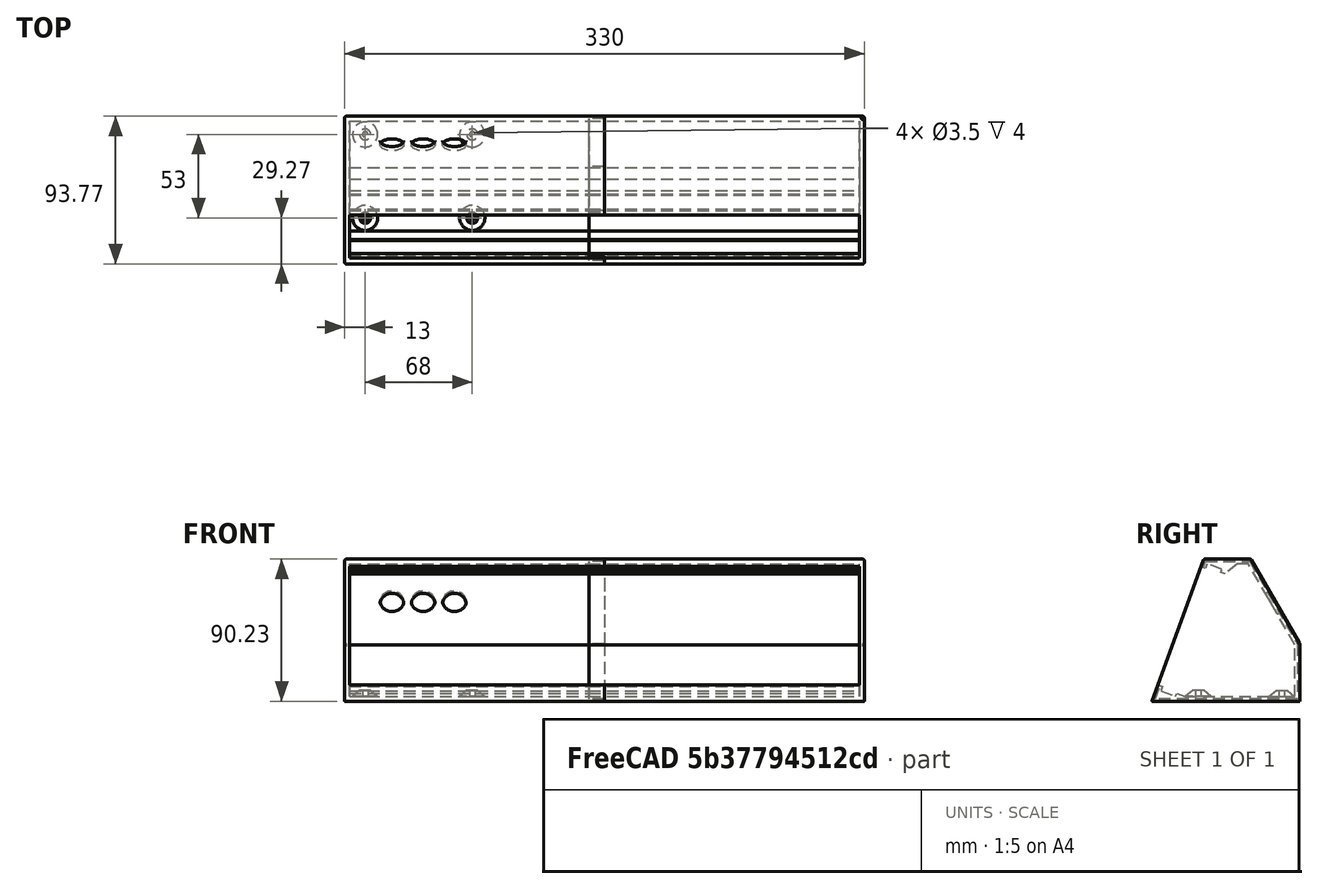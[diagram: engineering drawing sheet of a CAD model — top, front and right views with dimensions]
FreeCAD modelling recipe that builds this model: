
FCSTD DOCUMENT  (FreeCAD 1.0R39109 (Git))
Label: Unibody
License: All rights reserved
LicenseURL: https://en.wikipedia.org/wiki/All_rights_reserved
objects: Sketcher::SketchObject×11, PartDesign::Plane×8, PartDesign::Pocket×6, PartDesign::Fillet×5, PartDesign::Body×3, PartDesign::SubShapeBinder×2, PartDesign::Mirrored×2, PartDesign::FeatureBase×2, Spreadsheet::Sheet×1, PartDesign::Pad×1, PartDesign::AdditiveCone×1, Mesh::Feature×1, PartDesign::Hole×1, PartDesign::MultiTransform×1
note: 87 computed .brp shape members not serialized (recipe doc carries the construction recipe); baked Part::Feature solids carry a one-line shape summary decoded from their .brp

FEATURE [Sketcher::SketchObject] Sketch  label="ProfileMasterSketch"
  ArcFitTolerance = 1e-06
  AttachmentSupport = -> [YZ_Plane]
  FullyConstrained = true
  MakeInternals = false
  MapMode = 5
  Placement = pos=(0,0,0) rot=(0.57735,0.57735,0.57735;2.0944rad)
  expr: Constraints[25] = 90 deg + <<HousingSS>>.screen_angle
  expr: Constraints[35] = <<HousingSS>>.case_thickness
  expr: Constraints[36] = <<HousingSS>>.case_thickness
  expr: Constraints[37] = <<HousingSS>>.case_thickness
  expr: Constraints[38] = <<HousingSS>>.case_thickness
  expr: Constraints[39] = <<HousingSS>>.case_thickness
  expr: Constraints[40] = <<HousingSS>>.case_thickness
  expr: Constraints[41] = <<HousingSS>>.case_thickness
  expr: Constraints[44] = <<HousingSS>>.case_thickness
  expr: Constraints[45] = <<HousingSS>>.case_thickness
  expr: Constraints[46] = 90 deg - <<HousingSS>>.screen_angle
  expr: Constraints[47] = <<HousingSS>>.screen_assembly_depth
  expr: Constraints[48] = <<HousingSS>>.screen_assembly_depth
  expr: Constraints[50] = <<HousingSS>>.back_support_face_height
  expr: Constraints[51] = <<HousingSS>>.back_support_face_height
  expr: Constraints[53] = <<HousingSS>>.case_thickness
  expr: Constraints[54] = <<HousingSS>>.screen_height
  expr: Constraints[56] = <<HousingSS>>.back_angle + 90 deg
  expr: Constraints[60] = <<HousingSS>>.case_thickness
  expr: Constraints[61] = <<HousingSS>>.case_thickness
  expr: Constraints[62] = <<HousingSS>>.case_thickness
  expr: Constraints[63] = <<HousingSS>>.top_depth
  expr: Constraints[64] = <<HousingSS>>.back_bay_depth
  expr: Constraints[66] = <<HousingSS>>.case_thickness
  sketch-geometry (24):
    g0: LineSegment StartX=-60.9314 StartY=90.2338 StartZ=0 EndX=-30.9314 EndY=90.2338 EndZ=0
    g1: LineSegment StartX=-30.9314 StartY=90.2338 StartZ=0 EndX=0 EndY=36.659 EndZ=0
    g2: LineSegment StartX=0 StartY=36.659 StartZ=0 EndX=0 EndY=0 EndZ=0
    g3: LineSegment StartX=0 StartY=0 StartZ=0 EndX=-93.7738 EndY=0 EndZ=0
    g4: LineSegment StartX=-3 StartY=35.8551 StartZ=0 EndX=-3 EndY=3 EndZ=0
    g5: LineSegment StartX=-88.2445 StartY=6.4202 StartZ=0 EndX=-87.2185 EndY=9.23928 EndZ=0
    g6: LineSegment StartX=-87.2185 StartY=9.23928 StartZ=0 EndX=-90.0376 EndY=10.2653 EndZ=0
    g7: LineSegment StartX=-90.0376 StartY=10.2653 StartZ=0 EndX=-93.7738 EndY=0 EndZ=0
    g8: LineSegment StartX=-58.8308 StartY=87.2338 StartZ=0 EndX=-59.8569 EndY=84.4147 EndZ=0
    g9: LineSegment StartX=-59.8569 StartY=84.4147 StartZ=0 EndX=-62.6759 EndY=85.4407 EndZ=0
    g10: LineSegment StartX=-78.8476 StartY=3 StartZ=0 EndX=-88.2445 EndY=6.4202 EndZ=0
    g11: LineSegment StartX=-78.1636 StartY=4.87939 StartZ=0 EndX=-78.8476 EndY=3 EndZ=0
    g12: LineSegment StartX=-93.7738 StartY=0 StartZ=0 EndX=-90.0376 EndY=10.2653 EndZ=0
    g13: LineSegment [constr] StartX=-90.0376 StartY=10.2653 StartZ=0 EndX=-62.6759 EndY=85.4407 EndZ=0
    g14: LineSegment StartX=-62.6759 StartY=85.4407 StartZ=0 EndX=-60.9314 EndY=90.2338 EndZ=0
    g15: LineSegment StartX=-50.1179 StartY=81.9342 StartZ=0 EndX=-49.4339 EndY=83.8136 EndZ=0
    g16: LineSegment StartX=-49.4339 StartY=83.8136 StartZ=0 EndX=-58.8308 EndY=87.2338 EndZ=0
    g17: LineSegment StartX=-32.6635 StartY=87.2338 StartZ=0 EndX=-3 EndY=35.8551 EndZ=0
    g18: LineSegment StartX=-3 StartY=3 StartZ=0 EndX=-73 EndY=3 EndZ=0
    g19: LineSegment StartX=-73 StartY=3 StartZ=0 EndX=-78.1636 EndY=4.87939 EndZ=0
    g20: LineSegment StartX=-39.7602 StartY=87.2338 StartZ=0 EndX=-32.6635 EndY=87.2338 EndZ=0
    g21: LineSegment [constr] StartX=-32.6635 StartY=87.2338 StartZ=0 EndX=-30.0654 EndY=88.7338 EndZ=0
    g22: LineSegment StartX=-50.1179 StartY=81.9342 StartZ=0 EndX=-47.2988 EndY=80.9081 EndZ=0
    g23: LineSegment StartX=-47.2988 StartY=80.9081 StartZ=0 EndX=-39.7602 EndY=87.2338 EndZ=0
  constraints (69):
    c: Horizontal(g0)
    c: Coincident(g0,g1)
    c: PointOnObject(g1,g-2)
    c: Coincident(g1,g2)
    c: Coincident(g2,g-1)
    c: Coincident(g2,g3)
    c: PointOnObject(g3,g-1)
    c: Coincident(g3,g12)
    c: Coincident(g14,g0)
    c: Coincident(g17,g4)
    c: Coincident(g4,g18)
    c: Coincident(g10,g5)
    c: Coincident(g5,g6)
    c: Coincident(g6,g7)
    c: Coincident(g7,g3)
    c: Coincident(g22,g15)
    c: Coincident(g16,g8)
    c: Coincident(g8,g9)
    c: Coincident(g11,g10)
    c: Coincident(g19,g11)
    c: Coincident(g12,g13)
    c: PointOnObject(g9,g12)
    c: Coincident(g13,g14)
    c: Coincident(g13,g9)
    c: Coincident(g12,g6)
    c: Angle(g14,g0) = 1.91986
    c: Angle(g13,g9) = 1.5708
    c: Parallel(g8,g14)
    c: Angle(g7,g6) = 1.5708
    c: Angle(g6,g5) = 1.5708
    c: Angle(g10,g5) = 1.5708
    c: Coincident(g15,g16)
    c: Coincident(g18,g19)
    c: Angle(g11,g10) = 1.5708
    c: Parallel(g17,g1)
    c: DistanceY(g17,g0) = 3
    c: DistanceX(g4,g1) = 3
    c: DistanceX(g4,g2) = 3
    c: DistanceY(g-1,g18) = 3
    c: DistanceY(g-1,g4) = 3
    c: Distance(g6) = 3
    c: Distance(g9) = 3
    c: Angle(g8,g16) = 1.5708
    c: Angle(g16,g15) = 1.5708
    c: DistanceY(g8,g0) = 3
    c: DistanceY(g-1,g10) = 3
    c: Angle(g3,g13) = 1.22173
    c: Distance(g10) = 10
    c: Distance(g16) = 10
    c: Angle(g11,g19) = 1.5708
    c: Distance(g11) = 2
    c: Distance(g15) = 2
    c: Coincident(g23,g20)
    c: DistanceY(g23,g0) = 3
    c: Distance(g13) = 80
    c: Coincident(g20,g17)
    c: Angle(g20,g17) = 2.0944
    c: Coincident(g21,g17)
    c: PointOnObject(g21,g1)
    c: Angle(g17,g21) = 1.5708
    c: Distance(g21) = 3
    c: Distance(g5) = 3
    c: Distance(g8) = 3
    c: Distance(g0) = 30
    c: Distance(g18) = 70
    c: Coincident(g22,g23)
    c: Distance(g22) = 3
    c: Angle(g22,g15) = 1.5708
    c: Angle(g23,g22) = 2.0944
FEATURE [Spreadsheet::Sheet] Spreadsheet  label="HousingSS"
  cells = B1='screen_angle; C1='case_thickness; D1='screen_assembly_depth; E1='screen_height; F1='back_support_face_height; G1='back_angle; H1='top_depth; I1='back_edge_height; J1='housing_width; K1='opening_width; L1='back_bay_depth; M1='split_offset; N1='screw_split_offset; O1='split_overlap; P1='split_middle; Q1='breakout_mount_diameter; R1='button_diameter; S1='button_spacing; T1='pin_pitch; U1='breakout_mount_support; V1='threaded_insert_diameter; W1='threaded_insert_depth; A2==hiddenref(Body.Configuration.String); B2(screen_angle)==.B3; C2(case_thickness)==.C3; D2(screen_assembly_depth)==.D3; E2(screen_height)==.E3; F2(back_support_face_height)==.F3; G2(back_angle)==.G3; H2(top_depth)==.H3; I2(back_edge_height)==.I3; J2(housing_width)==.J3; K2(opening_width)==.K3; L2(back_bay_depth)==.L3; M2(split_offset)==.M3; N2(screw_split_offset)==.N3; O2(split_overlap)==.O3; P2(split_middle)==.P3; Q2(breakout_mount_diameter)==.Q3; R2(button_diameter)==.R3; S2(button_spacing)==.S3; T2(pin_pitch)==.T3; U2(breakout_mount_support)==.U3; V2(threaded_insert_diameter)==.V3; W2(threaded_insert_depth)==.W3; A3='A; B3==20 deg; C3==3 mm; D3==1 cm; E3==80 mm; F3==2 mm; G3==30 deg; H3==3 cm; I3==30 mm; J3==33 cm; K3==housing_width - case_thickness * 2; L3==70 mm; M3==housing_width / 2; N3==10 mm; O3==1 cm; P3==split_offset + split_overlap / 2; Q3==3 mm; R3==15 mm; S3==button_diameter + mod(button_diameter; pin_pitch) * 1 mm + pin_pitch; T3==2.54 mm; U3==4 mm; V3==5 mm; W3==4 mm
  expr: .cells.Bind.B2.ZZ2 = tuple(.cells; <<B>> + str(hiddenref(Body.Configuration) + 3); <<ZZ>> + str(hiddenref(Body.Configuration) + 3))
FEATURE [Sketcher::SketchObject] Sketch001  label="OuterBodySketch"
  ArcFitTolerance = 1e-06
  AttachmentSupport = -> [YZ_Plane]
  ExternalGeometry = -> [Sketch]
  FullyConstrained = true
  MakeInternals = false
  MapMode = 5
  Placement = pos=(0,0,0) rot=(0.57735,0.57735,0.57735;2.0944rad)
  sketch-geometry (5):
    g0: LineSegment StartX=-60.9314 StartY=90.2338 StartZ=0 EndX=-93.7738 EndY=0 EndZ=0
    g1: LineSegment StartX=-93.7738 StartY=0 StartZ=0 EndX=0 EndY=0 EndZ=0
    g2: LineSegment StartX=0 StartY=0 StartZ=0 EndX=0 EndY=36.659 EndZ=0
    g3: LineSegment StartX=0 StartY=36.659 StartZ=0 EndX=-30.9314 EndY=90.2338 EndZ=0
    g4: LineSegment StartX=-30.9314 StartY=90.2338 StartZ=0 EndX=-60.9314 EndY=90.2338 EndZ=0
  constraints (10):
    c: Coincident(g0,g-3)
    c: Coincident(g0,g-4)
    c: Coincident(g0,g1)
    c: Coincident(g1,g-1)
    c: Coincident(g1,g2)
    c: Coincident(g2,g-5)
    c: Coincident(g2,g3)
    c: Coincident(g3,g-6)
    c: Coincident(g3,g4)
    c: Coincident(g4,g0)
FEATURE [PartDesign::Pad] Pad  label="OuterBody"
  Direction = (1,0,0)
  Length = 330
  Length2 = 10
  Placement = pos=(0,0,0) rot=(1,1,1;2.0944rad)
  Profile = -> Sketch001
  ReferenceAxis = -> Sketch001 [N_Axis]
  Refine = true
  Suppressed = false
  Type = 0
  expr: Length = <<HousingSS>>.housing_width
FEATURE [PartDesign::Plane] DatumPlane  label="InnerWallPlane"
  AttachmentOffset = pos=(0,0,3) rot=(0,0,1;0rad)
  AttachmentSupport = -> [YZ_Plane]
  Length = 142.172
  MapMode = 5
  Placement = pos=(3,0,0) rot=(0.57735,0.57735,0.57735;2.0944rad)
  ResizeMode = 0
  Width = 138.632
  expr: .AttachmentOffset.Base.z = <<HousingSS>>.case_thickness
FEATURE [Sketcher::SketchObject] Sketch002  label="InnerOpeningSketch"
  ArcFitTolerance = 1e-06
  AttachmentSupport = -> [DatumPlane]
  ExternalGeometry = -> [Sketch]
  FullyConstrained = true
  MakeInternals = false
  MapMode = 5
  Placement = pos=(3,0,0) rot=(0.57735,0.57735,0.57735;2.0944rad)
  sketch-geometry (16):
    g0: LineSegment StartX=-62.6759 StartY=85.4407 StartZ=0 EndX=-90.0376 EndY=10.2653 EndZ=0
    g1: LineSegment StartX=-90.0376 StartY=10.2653 StartZ=0 EndX=-87.2185 EndY=9.23928 EndZ=0
    g2: LineSegment StartX=-87.2185 StartY=9.23928 StartZ=0 EndX=-88.2445 EndY=6.4202 EndZ=0
    g3: LineSegment StartX=-88.2445 StartY=6.4202 StartZ=0 EndX=-78.8476 EndY=3 EndZ=0
    g4: LineSegment StartX=-78.8476 StartY=3 StartZ=0 EndX=-78.1636 EndY=4.87939 EndZ=0
    g5: LineSegment StartX=-78.1636 StartY=4.87939 StartZ=0 EndX=-73 EndY=3 EndZ=0
    g6: LineSegment StartX=-73 StartY=3 StartZ=0 EndX=-3 EndY=3 EndZ=0
    g7: LineSegment StartX=-3 StartY=3 StartZ=0 EndX=-3 EndY=35.8551 EndZ=0
    g8: LineSegment StartX=-3 StartY=35.8551 StartZ=0 EndX=-32.6635 EndY=87.2338 EndZ=0
    g9: LineSegment StartX=-32.6635 StartY=87.2338 StartZ=0 EndX=-39.7602 EndY=87.2338 EndZ=0
    g10: LineSegment StartX=-50.1179 StartY=81.9342 StartZ=0 EndX=-49.4339 EndY=83.8136 EndZ=0
    g11: LineSegment StartX=-49.4339 StartY=83.8136 StartZ=0 EndX=-58.8308 EndY=87.2338 EndZ=0
    g12: LineSegment StartX=-58.8308 StartY=87.2338 StartZ=0 EndX=-59.8569 EndY=84.4147 EndZ=0
    g13: LineSegment StartX=-59.8569 StartY=84.4147 StartZ=0 EndX=-62.6759 EndY=85.4407 EndZ=0
    g14: LineSegment StartX=-39.7602 StartY=87.2338 StartZ=0 EndX=-47.2988 EndY=80.9081 EndZ=0
    g15: LineSegment StartX=-47.2988 StartY=80.9081 StartZ=0 EndX=-50.1179 EndY=81.9342 EndZ=0
  constraints (32):
    c: Coincident(g0,g-16)
    c: Coincident(g0,g-4)
    c: Coincident(g0,g1)
    c: Coincident(g1,g-5)
    c: Coincident(g1,g2)
    c: Coincident(g2,g-6)
    c: Coincident(g2,g3)
    c: Coincident(g3,g-7)
    c: Coincident(g3,g4)
    c: Coincident(g4,g-8)
    c: Coincident(g4,g5)
    c: Coincident(g5,g-9)
    c: Coincident(g5,g6)
    c: Coincident(g6,g-10)
    c: Coincident(g6,g7)
    c: Coincident(g7,g-11)
    c: Coincident(g7,g8)
    c: Coincident(g8,g-12)
    c: Coincident(g8,g9)
    c: Coincident(g15,g-13)
    c: Coincident(g15,g10)
    c: Coincident(g10,g-14)
    c: Coincident(g10,g11)
    c: Coincident(g11,g-15)
    c: Coincident(g11,g12)
    c: Coincident(g12,g-3)
    c: Coincident(g12,g13)
    c: Coincident(g13,g0)
    c: Coincident(g9,g-18)
    c: Coincident(g14,g9)
    c: Coincident(g14,g15)
    c: Coincident(g14,g-17)
FEATURE [PartDesign::Pocket] Pocket
  BaseFeature = -> Pad
  Direction = (-1,0,0)
  Length = 324
  Length2 = 5
  Placement = pos=(0,0,0) rot=(1,1,1;2.0944rad)
  Profile = -> Sketch002
  ReferenceAxis = -> Sketch002 [N_Axis]
  Refine = true
  Reversed = true
  Suppressed = false
  Type = 0
  expr: Length = <<HousingSS>>.opening_width
FEATURE [PartDesign::Plane] DatumPlane001  label="BackSlopeDatumPlane"
  AttachmentOffset = pos=(0,0,0) rot=(1,0,0;1.5708rad)
  AttachmentSupport = -> [Sketch]
  Length = 67.8428
  MapMode = 7
  Placement = pos=(0,-30.9314,90.2338) rot=(1,0,0;2.0944rad)
  ResizeMode = 0
  Width = 177.025
FEATURE [Sketcher::SketchObject] Sketch003  label="SplitCutSketch"
  ArcFitTolerance = 1e-06
  AttachmentSupport = -> [YZ_Plane]
  ExternalGeometry = -> [Sketch]
  FullyConstrained = true
  MakeInternals = false
  MapMode = 5
  Placement = pos=(0,0,0) rot=(0.57735,0.57735,0.57735;2.0944rad)
  expr: Constraints[23] = Sketch.Constraints[25]
  expr: Constraints[25] = Sketch.Constraints[30]
  expr: Constraints[28] = Sketch.Constraints[33]
  expr: Constraints[30] = Sketch.Constraints[35]
  expr: Constraints[31] = Sketch.Constraints[36]
  expr: Constraints[32] = Sketch.Constraints[37]
  expr: Constraints[33] = Sketch.Constraints[38]
  expr: Constraints[34] = Sketch.Constraints[42]
  expr: Constraints[35] = Sketch.Constraints[43]
  expr: Constraints[36] = Sketch.Constraints[44]
  expr: Constraints[37] = Sketch.Constraints[45]
  expr: Constraints[38] = Sketch.Constraints[46]
  expr: Constraints[39] = Sketch.Constraints[47]
  expr: Constraints[40] = Sketch.Constraints[48]
  expr: Constraints[41] = Sketch.Constraints[49]
  expr: Constraints[42] = Sketch.Constraints[50]
  expr: Constraints[43] = Sketch.Constraints[51]
  expr: Constraints[44] = Sketch.Constraints[53]
  expr: Constraints[45] = Sketch.Constraints[54]
  expr: Constraints[47] = Sketch.Constraints[56]
  expr: Constraints[50] = Sketch.Constraints[59]
  expr: Constraints[51] = Sketch.Constraints[60]
  expr: Constraints[52] = Sketch.Constraints[61]
  expr: Constraints[53] = Sketch.Constraints[62]
  expr: Constraints[54] = Sketch.Constraints[63]
  expr: Constraints[55] = Sketch.Constraints[64]
  expr: Constraints[92] = <<HousingSS>>.case_thickness / 2
  sketch-geometry (42):
    g0: LineSegment StartX=-60.9314 StartY=90.2338 StartZ=0 EndX=-30.9314 EndY=90.2338 EndZ=0
    g1: LineSegment StartX=-30.9314 StartY=90.2338 StartZ=0 EndX=0 EndY=36.659 EndZ=0
    g2: LineSegment StartX=0 StartY=36.659 StartZ=0 EndX=0 EndY=0 EndZ=0
    g3: LineSegment StartX=0 StartY=0 StartZ=0 EndX=-93.7738 EndY=0 EndZ=0
    g4: LineSegment StartX=-3 StartY=35.8551 StartZ=0 EndX=-3 EndY=3 EndZ=0
    g5: LineSegment StartX=-88.2445 StartY=6.4202 StartZ=0 EndX=-87.2185 EndY=9.23928 EndZ=0
    g6: LineSegment StartX=-90.0376 StartY=10.2653 StartZ=0 EndX=-93.7738 EndY=0 EndZ=0
    g7: LineSegment StartX=-58.8308 StartY=87.2338 StartZ=0 EndX=-59.8569 EndY=84.4147 EndZ=0
    g8: LineSegment StartX=-78.8476 StartY=3 StartZ=0 EndX=-88.2445 EndY=6.4202 EndZ=0
    g9: LineSegment StartX=-78.1636 StartY=4.87939 StartZ=0 EndX=-78.8476 EndY=3 EndZ=0
    g10: LineSegment StartX=-93.7738 StartY=0 StartZ=0 EndX=-90.0376 EndY=10.2653 EndZ=0
    g11: LineSegment [constr] StartX=-90.0376 StartY=10.2653 StartZ=0 EndX=-62.6759 EndY=85.4407 EndZ=0
    g12: LineSegment StartX=-62.6759 StartY=85.4407 StartZ=0 EndX=-60.9314 EndY=90.2338 EndZ=0
    g13: LineSegment StartX=-50.1179 StartY=81.9342 StartZ=0 EndX=-49.4339 EndY=83.8136 EndZ=0
    g14: LineSegment StartX=-49.4339 StartY=83.8136 StartZ=0 EndX=-58.8308 EndY=87.2338 EndZ=0
    g15: LineSegment StartX=-32.6635 StartY=87.2338 StartZ=0 EndX=-3 EndY=35.8551 EndZ=0
    g16: LineSegment StartX=-3 StartY=3 StartZ=0 EndX=-73 EndY=3 EndZ=0
    g17: LineSegment StartX=-73 StartY=3 StartZ=0 EndX=-78.1636 EndY=4.87939 EndZ=0
    g18: LineSegment StartX=-47.2988 StartY=80.9081 StartZ=0 EndX=-39.7602 EndY=87.2338 EndZ=0
    g19: LineSegment StartX=-39.7602 StartY=87.2338 StartZ=0 EndX=-32.6635 EndY=87.2338 EndZ=0
    g20: LineSegment [constr] StartX=-32.6635 StartY=87.2338 StartZ=0 EndX=-30.0654 EndY=88.7338 EndZ=0
    g21: LineSegment StartX=-59.8569 StartY=84.4147 StartZ=0 EndX=-61.2664 EndY=84.9277 EndZ=0
    g22: LineSegment StartX=-61.2664 StartY=84.9277 StartZ=0 EndX=-62.6759 EndY=85.4407 EndZ=0
    g23: LineSegment StartX=-87.2185 StartY=9.23928 StartZ=0 EndX=-88.628 EndY=9.75231 EndZ=0
    g24: LineSegment StartX=-88.628 StartY=9.75231 StartZ=0 EndX=-90.0376 EndY=10.2653 EndZ=0
    g25: LineSegment [constr] StartX=-58.8308 StartY=87.2338 StartZ=0 EndX=-59.8811 EndY=88.7338 EndZ=0
    g26: LineSegment [constr] StartX=-59.8811 StartY=88.7338 StartZ=0 EndX=-60.9314 EndY=90.2338 EndZ=0
    g27: LineSegment [constr] StartX=-32.6635 StartY=87.2338 StartZ=0 EndX=-31.7975 EndY=88.7338 EndZ=0
    g28: LineSegment [constr] StartX=-31.7975 StartY=88.7338 StartZ=0 EndX=-30.9314 EndY=90.2338 EndZ=0
    g29: LineSegment [constr] StartX=-3 StartY=35.8551 StartZ=0 EndX=-1.5 EndY=36.257 EndZ=0
    g30: LineSegment [constr] StartX=-1.5 StartY=36.257 StartZ=0 EndX=0 EndY=36.659 EndZ=0
    g31: LineSegment StartX=-61.2664 StartY=84.9277 StartZ=0 EndX=-59.8811 EndY=88.7338 EndZ=0
    g32: LineSegment StartX=-59.8811 StartY=88.7338 StartZ=0 EndX=-31.7975 EndY=88.7338 EndZ=0
    g33: LineSegment StartX=-31.7975 StartY=88.7338 StartZ=0 EndX=-1.5 EndY=36.257 EndZ=0
    g34: LineSegment StartX=-1.5 StartY=36.257 StartZ=0 EndX=-1.5 EndY=1.5 EndZ=0
    g35: LineSegment StartX=-91.6316 StartY=1.5 StartZ=0 EndX=-88.628 EndY=9.75231 EndZ=0
    g36: LineSegment [constr] StartX=-88.628 StartY=9.75231 StartZ=0 EndX=-91.6316 EndY=1.5 EndZ=0
    g37: LineSegment [constr] StartX=-91.6316 StartY=1.5 StartZ=0 EndX=-92.1776 EndY=0 EndZ=0
    g38: LineSegment StartX=-91.6316 StartY=1.5 StartZ=0 EndX=-1.5 EndY=1.5 EndZ=0
    g39: LineSegment [constr] StartX=-3 StartY=3 StartZ=0 EndX=-1.5 EndY=1.5 EndZ=0
    g40: LineSegment [constr] StartX=-1.5 StartY=1.5 StartZ=0 EndX=0 EndY=0 EndZ=0
    g41: LineSegment StartX=-50.1179 StartY=81.9342 StartZ=0 EndX=-47.2988 EndY=80.9081 EndZ=0
  constraints (106):
    c: Horizontal(g0)
    c: Coincident(g0,g1)
    c: PointOnObject(g1,g-2)
    c: Coincident(g1,g2)
    c: Coincident(g2,g3)
    c: PointOnObject(g3,g-1)
    c: Coincident(g3,g10)
    c: Coincident(g12,g0)
    c: Coincident(g15,g4)
    c: Coincident(g4,g16)
    c: Coincident(g8,g5)
    c: Coincident(g5,g23)
    c: Coincident(g24,g6)
    c: Coincident(g6,g3)
    c: Coincident(g14,g7)
    c: Coincident(g7,g21)
    c: Coincident(g9,g8)
    c: Coincident(g17,g9)
    c: Coincident(g10,g11)
    c: PointOnObject(g22,g10)
    c: Coincident(g11,g12)
    c: Coincident(g11,g22)
    c: Coincident(g10,g24)
    c: Angle(g12,g0) = 1.91986
    c: Parallel(g7,g12)
    c: Angle(g8,g5) = 1.5708
    c: Coincident(g13,g14)
    c: Coincident(g16,g17)
    c: Angle(g9,g8) = 1.5708
    c: Parallel(g15,g1)
    c: DistanceY(g15,g0) = 3
    c: DistanceX(g4,g1) = 3
    c: DistanceX(g4,g2) = 3
    c: DistanceY(g-1,g16) = 3
    c: Angle(g7,g14) = 1.5708
    c: Angle(g14,g13) = 1.5708
    c: DistanceY(g7,g0) = 3
    c: DistanceY(g-1,g8) = 3
    c: Angle(g3,g11) = 1.22173
    c: Distance(g8) = 10
    c: Distance(g14) = 10
    c: Angle(g9,g17) = 1.5708
    c: Distance(g9) = 2
    c: Distance(g13) = 2
    c: DistanceY(g18,g0) = 3
    c: Distance(g11) = 80
    c: Coincident(g19,g15)
    c: Angle(g19,g15) = 2.0944
    c: Coincident(g20,g15)
    c: PointOnObject(g20,g1)
    c: Angle(g15,g20) = 1.5708
    c: Distance(g20) = 3
    c: Distance(g5) = 3
    c: Distance(g7) = 3
    c: Distance(g0) = 30
    c: Distance(g16) = 70
    c: Coincident(g21,g22)
    c: Distance(g21,g22) = 3
    c: Equal(g21,g22)
    c: Distance(g23,g24) = 3
    c: Equal(g23,g24)
    c: Angle(g23,g5) = 1.5708
    c: Angle(g7,g21) = 1.5708
    c: Angle(g22,g12) = 1.5708
    c: Tangent(g23,g24) = -1.5708
    c: Coincident(g25,g7)
    c: Coincident(g26,g0)
    c: Tangent(g25,g26) = -1.5708
    c: Equal(g26,g25)
    c: Coincident(g27,g15)
    c: Coincident(g28,g0)
    c: Tangent(g27,g28) = -1.5708
    c: Equal(g27,g28)
    c: Coincident(g29,g4)
    c: Coincident(g30,g1)
    c: Tangent(g29,g30) = -1.5708
    c: Equal(g29,g30)
    c: Coincident(g21,g31)
    c: Coincident(g31,g25)
    c: Coincident(g31,g32)
    c: Coincident(g32,g27)
    c: Coincident(g32,g33)
    c: Coincident(g33,g29)
    c: Coincident(g33,g34)
    c: Coincident(g35,g23)
    c: Coincident(g-1,g2)
    c: Angle(g4,g16) = 1.5708
    c: Coincident(g36,g23)
    c: PointOnObject(g37,g3)
    c: Coincident(g36,g37)
    c: Parallel(g36,g6)
    c: Parallel(g37,g6)
    c: DistanceY(g3,g36) = 1.5
    c: Coincident(g35,g36)
    c: Coincident(g38,g35)
    c: Coincident(g38,g34)
    c: Horizontal(g38)
    c: Coincident(g39,g4)
    c: Coincident(g40,g2)
    c: Tangent(g39,g40) = -1.5708
    c: Coincident(g34,g39)
    c: Coincident(g19,g-3)
    c: Coincident(g18,g19)
    c: Coincident(g18,g-4)
    c: Coincident(g41,g13)
    c: Coincident(g41,g18)
FEATURE [PartDesign::SubShapeBinder] Binder
  BindCopyOnChange = 0
  BindMode = 0
  ClaimChildren = false
  Context = -> Body001 [Binder.]
  Fuse = false
  MakeFace = true
  OffsetFill = false
  OffsetIntersection = false
  OffsetJoinType = 0
  OffsetOpenResult = false
  PartialLoad = false
  Refine = true
  Relative = true
  Support = -> [Body[Sketch003.]]
  _Version = 2
FEATURE [PartDesign::SubShapeBinder] Binder001
  BindCopyOnChange = 0
  BindMode = 0
  ClaimChildren = false
  Context = -> Body002 [Binder001.]
  Fuse = false
  MakeFace = true
  OffsetFill = false
  OffsetIntersection = false
  OffsetJoinType = 0
  OffsetOpenResult = false
  PartialLoad = false
  Refine = true
  Relative = true
  Support = -> [Body[Sketch003.]]
  _Version = 2
FEATURE [PartDesign::Plane] DatumPlane004  label="InnerBottomPlane"
  AttachmentOffset = pos=(0,0,3) rot=(0,0,1;0rad)
  AttachmentSupport = -> [XY_Plane]
  Length = 65.4126
  MapMode = 5
  Placement = pos=(0,0,3) rot=(0,0,1;0rad)
  ResizeMode = 0
  Width = 134.186
  expr: .AttachmentOffset.Base.z = <<HousingSS>>.case_thickness
FEATURE [Sketcher::SketchObject] Sketch008  label="BottomMasterSketch"
  ArcFitTolerance = 1e-06
  AttachmentSupport = -> [DatumPlane004]
  ExternalGeometry = -> [Sketch002,Pocket]
  FullyConstrained = true
  MakeInternals = false
  MapMode = 5
  Placement = pos=(0,0,3) rot=(0,0,1;0rad)
  expr: Constraints[27] = <<HousingSS>>.breakout_mount_diameter
  expr: Constraints[28] = <<HousingSS>>.breakout_mount_diameter
  expr: Constraints[29] = 1 cm
  expr: Constraints[31] = <<HousingSS>>.breakout_mount_support
  expr: Constraints[33] = <<HousingSS>>.breakout_mount_support
  expr: Constraints[35] = <<HousingSS>>.breakout_mount_support
  expr: Constraints[37] = <<HousingSS>>.breakout_mount_support
  sketch-geometry (24):
    g0: LineSegment StartX=327 StartY=-3 StartZ=0 EndX=3 EndY=-3 EndZ=0
    g1: LineSegment StartX=3 StartY=-3 StartZ=0 EndX=3 EndY=-73 EndZ=0
    g2: LineSegment StartX=3 StartY=-73 StartZ=0 EndX=327 EndY=-73 EndZ=0
    g3: LineSegment StartX=327 StartY=-73 StartZ=0 EndX=327 EndY=-3 EndZ=0
    g4: Circle CenterX=13 CenterY=-11.5 CenterZ=0 NormalX=0 NormalY=0 NormalZ=1 AngleXU=0 Radius=1.5
    g5: Circle CenterX=13 CenterY=-64.5 CenterZ=0 NormalX=0 NormalY=0 NormalZ=1 AngleXU=0 Radius=1.5
    g6: Circle CenterX=81 CenterY=-11.4999 CenterZ=0 NormalX=0 NormalY=0 NormalZ=1 AngleXU=0 Radius=1.5
    g7: Circle CenterX=81 CenterY=-64.5 CenterZ=0 NormalX=0 NormalY=0 NormalZ=1 AngleXU=0 Radius=1.5
    g8: LineSegment [constr] StartX=13 StartY=-11.5 StartZ=0 EndX=13 EndY=-3 EndZ=0
    g9: LineSegment [constr] StartX=13 StartY=-64.5 StartZ=0 EndX=13 EndY=-73 EndZ=0
    g10: Circle CenterX=13 CenterY=-64.5 CenterZ=0 NormalX=0 NormalY=0 NormalZ=1 AngleXU=0 Radius=2
    g11: Circle CenterX=13 CenterY=-11.5 CenterZ=0 NormalX=0 NormalY=0 NormalZ=1 AngleXU=0 Radius=2
    g12: Circle CenterX=81 CenterY=-11.4999 CenterZ=0 NormalX=0 NormalY=0 NormalZ=1 AngleXU=0 Radius=2
    g13: Circle CenterX=81 CenterY=-64.5 CenterZ=0 NormalX=0 NormalY=0 NormalZ=1 AngleXU=0 Radius=2
    g14: LineSegment [constr] StartX=13 StartY=-11.5 StartZ=0 EndX=13 EndY=-38 EndZ=0
    g15: LineSegment [constr] StartX=13 StartY=-38 StartZ=0 EndX=13 EndY=-64.5 EndZ=0
    g16: LineSegment [constr] StartX=81 StartY=-64.5 StartZ=0 EndX=81 EndY=-38 EndZ=0
    g17: LineSegment [constr] StartX=81 StartY=-38 StartZ=0 EndX=81 EndY=-11.4999 EndZ=0
    g18: LineSegment StartX=13 StartY=-38 StartZ=0 EndX=81 EndY=-38 EndZ=0
    g19: LineSegment [constr] StartX=81 StartY=-11.4999 StartZ=0 EndX=47 EndY=-11.4999 EndZ=0
    g20: LineSegment [constr] StartX=47 StartY=-11.4999 StartZ=0 EndX=13 EndY=-11.5 EndZ=0
    g21: LineSegment [constr] StartX=13 StartY=-64.5 StartZ=0 EndX=47 EndY=-64.5 EndZ=0
    g22: LineSegment [constr] StartX=47 StartY=-64.5 StartZ=0 EndX=81 EndY=-64.5 EndZ=0
    g23: LineSegment StartX=47 StartY=-11.4999 StartZ=0 EndX=47 EndY=-64.5 EndZ=0
  constraints (60):
    c: Coincident(g0,g1)
    c: Coincident(g1,g2)
    c: Coincident(g2,g3)
    c: Coincident(g3,g0)
    c: Horizontal(g0)
    c: Horizontal(g2)
    c: Vertical(g1)
    c: Vertical(g3)
    c: Coincident(g0,g-5)
    c: Coincident(g1,g-3)
    c: Coincident(g14,g4)
    c: Coincident(g15,g5)
    c: Coincident(g21,g5)
    c: Coincident(g22,g7)
    c: Coincident(g22,g16)
    c: Coincident(g17,g6)
    c: Coincident(g17,g19)
    c: Coincident(g20,g4)
    c: Coincident(g8,g4)
    c: PointOnObject(g8,g0)
    c: Vertical(g8)
    c: Coincident(g9,g5)
    c: PointOnObject(g9,g2)
    c: Vertical(g9)
    c: Equal(g8,g9)
    c: Diameter(g7) = 3
    c: Diameter(g6) = 3
    c: Diameter(g4) = 3
    c: Diameter(g5) = 3
    c: Distance(g4,g1) = 10
    c: Coincident(g10,g5)
    c: Diameter(g10) = 4
    c: Coincident(g11,g4)
    c: Diameter(g11) = 4
    c: Coincident(g12,g6)
    c: Diameter(g12) = 4
    c: Coincident(g13,g7)
    c: Diameter(g13) = 4
    c: Coincident(g14,g15)
    c: Vertical(g14)
    c: Vertical(g15)
    c: Distance(g14,g15) = 53
    c: Coincident(g16,g17)
    c: Coincident(g18,g14)
    c: Coincident(g18,g16)
    c: Horizontal(g18)
    c: Coincident(g19,g20)
    c: Coincident(g21,g22)
    c: Horizontal(g21)
    c: Horizontal(g22)
    c: Distance(g21,g22) = 68
    c: Coincident(g23,g19)
    c: Coincident(g23,g21)
    c: Vertical(g23)
    c: Equal(g14,g15)
    c: Equal(g22,g21)
    c: Angle(g19,g17) = 1.5708
    c: Distance(g20) = 34
    c: Angle(g16,g22) = 1.5708
    c: Angle(g23,g19) = 1.5708
FEATURE [PartDesign::Plane] DatumPlane005  label="TopOuterPlane"
  AttachmentOffset = pos=(0,0,100) rot=(1,0,0;1.5708rad)
  AttachmentSupport = -> [Sketch]
  Length = 69.2837
  MapMode = 7
  Placement = pos=(0,-160.931,90.2338) rot=(1,0,0;3.14159rad)
  ResizeMode = 0
  Width = 205.215
FEATURE [Sketcher::SketchObject] Sketch009  label="BackSlopeMasterSketch"
  ArcFitTolerance = 1e-06
  AttachmentSupport = -> [DatumPlane001]
  ExternalGeometry = -> [Sketch]
  FullyConstrained = true
  MakeInternals = false
  MapMode = 5
  Placement = pos=(0,-30.9314,90.2338) rot=(1,0,0;2.0944rad)
  expr: Constraints[35] = <<HousingSS>>.button_diameter
  expr: Constraints[36] = <<HousingSS>>.button_diameter
  expr: Constraints[37] = <<HousingSS>>.button_diameter
  expr: Constraints[39] = <<HousingSS>>.button_spacing
  expr: Constraints[41] = <<HousingSS>>.threaded_insert_diameter
  expr: Constraints[42] = <<HousingSS>>.threaded_insert_diameter
  expr: Constraints[43] = <<HousingSS>>.threaded_insert_diameter
  expr: Constraints[44] = <<HousingSS>>.threaded_insert_diameter
  expr: Constraints[60] = 2.54 mm * 3
  expr: Constraints[68] = 2.54 mm * 3
  expr: Constraints[9] = <<HousingSS>>.housing_width
  sketch-geometry (27):
    g0: LineSegment StartX=0 StartY=-61.8629 StartZ=0 EndX=330 EndY=-61.8629 EndZ=0
    g1: LineSegment StartX=330 StartY=-61.8629 StartZ=0 EndX=330 EndY=0 EndZ=0
    g2: LineSegment StartX=330 StartY=0 StartZ=0 EndX=0 EndY=0 EndZ=0
    g3: LineSegment StartX=0 StartY=0 StartZ=0 EndX=0 EndY=-61.8629 EndZ=0
    g4: Circle CenterX=30 CenterY=-30.9314 CenterZ=0 NormalX=0 NormalY=0 NormalZ=1 AngleXU=0 Radius=7.5
    g5: Circle CenterX=49.84 CenterY=-30.9314 CenterZ=0 NormalX=0 NormalY=0 NormalZ=1 AngleXU=0 Radius=7.5
    g6: Circle CenterX=69.68 CenterY=-30.9314 CenterZ=0 NormalX=0 NormalY=0 NormalZ=1 AngleXU=0 Radius=7.5
    g7: LineSegment [constr] StartX=30 StartY=-61.8629 StartZ=0 EndX=30 EndY=-30.9314 EndZ=0
    g8: LineSegment [constr] StartX=30 StartY=-30.9314 StartZ=0 EndX=30 EndY=0 EndZ=0
    g9: LineSegment [constr] StartX=49.84 StartY=-61.8629 StartZ=0 EndX=49.84 EndY=-30.9314 EndZ=0
    g10: LineSegment [constr] StartX=49.84 StartY=-30.9314 StartZ=0 EndX=49.84 EndY=0 EndZ=0
    g11: LineSegment [constr] StartX=69.68 StartY=-61.8629 StartZ=0 EndX=69.68 EndY=-30.9314 EndZ=0
    g12: LineSegment [constr] StartX=69.68 StartY=-30.9314 StartZ=0 EndX=69.68 EndY=0 EndZ=0
    g13: LineSegment [constr] StartX=69.68 StartY=-30.9314 StartZ=0 EndX=49.84 EndY=-30.9314 EndZ=0
    g14: LineSegment [constr] StartX=49.84 StartY=-30.9314 StartZ=0 EndX=30 EndY=-30.9314 EndZ=0
    g15: Circle CenterX=22.38 CenterY=-50.9314 CenterZ=0 NormalX=0 NormalY=0 NormalZ=1 AngleXU=0 Radius=2.5
    g16: Circle CenterX=22.38 CenterY=-10.9314 CenterZ=0 NormalX=0 NormalY=0 NormalZ=1 AngleXU=0 Radius=2.5
    g17: Circle CenterX=77.3 CenterY=-10.9314 CenterZ=0 NormalX=0 NormalY=0 NormalZ=1 AngleXU=0 Radius=2.5
    g18: Circle CenterX=77.3 CenterY=-50.9314 CenterZ=0 NormalX=0 NormalY=0 NormalZ=1 AngleXU=0 Radius=2.5
    g19: LineSegment [constr] StartX=22.38 StartY=-50.9314 StartZ=0 EndX=22.38 EndY=-10.9314 EndZ=0
    g20: LineSegment [constr] StartX=22.38 StartY=-10.9314 StartZ=0 EndX=77.3 EndY=-10.9314 EndZ=0
    g21: LineSegment [constr] StartX=77.3 StartY=-10.9314 StartZ=0 EndX=77.3 EndY=-50.9314 EndZ=0
    g22: LineSegment [constr] StartX=77.3 StartY=-50.9314 StartZ=0 EndX=22.38 EndY=-50.9314 EndZ=0
    g23: LineSegment [constr] StartX=22.38 StartY=-50.9314 StartZ=0 EndX=30 EndY=-30.9314 EndZ=0
    g24: LineSegment [constr] StartX=30 StartY=-30.9314 StartZ=0 EndX=22.38 EndY=-10.9314 EndZ=0
    g25: LineSegment [constr] StartX=77.3 StartY=-50.9314 StartZ=0 EndX=69.68 EndY=-30.9314 EndZ=0
    g26: LineSegment [constr] StartX=69.68 StartY=-30.9314 StartZ=0 EndX=77.3 EndY=-10.9314 EndZ=0
  constraints (69):
    c: Coincident(g0,g1)
    c: Coincident(g1,g2)
    c: Coincident(g2,g3)
    c: Coincident(g3,g0)
    c: Horizontal(g0)
    c: Horizontal(g2)
    c: Vertical(g1)
    c: Coincident(g0,g-3)
    c: Coincident(g-1,g2)
    c: Distance(g2) = 330
    c: PointOnObject(g7,g0)
    c: Coincident(g7,g4)
    c: Vertical(g7)
    c: Coincident(g7,g8)
    c: PointOnObject(g8,g2)
    c: Vertical(g8)
    c: PointOnObject(g9,g0)
    c: Coincident(g9,g5)
    c: Coincident(g9,g10)
    c: PointOnObject(g10,g2)
    c: Vertical(g10)
    c: PointOnObject(g11,g0)
    c: Coincident(g11,g6)
    c: Coincident(g11,g12)
    c: PointOnObject(g12,g2)
    c: Vertical(g12)
    c: Coincident(g13,g6)
    c: Coincident(g13,g5)
    c: Horizontal(g13)
    c: Coincident(g13,g14)
    c: Coincident(g14,g4)
    c: Horizontal(g14)
    c: Angle(g0,g9) = 1.5708
    c: Angle(g0,g11) = 1.5708
    c: Equal(g8,g7)
    c: Diameter(g6) = 15
    c: Diameter(g5) = 15
    c: Diameter(g4) = 15
    c: Equal(g14,g13)
    c: Distance(g13) = 19.84
    c: DistanceX(g-1,g4) = 30
    c: Diameter(g18) = 5
    c: Diameter(g17) = 5
    c: Diameter(g16) = 5
    c: Diameter(g15) = 5
    c: Coincident(g19,g15)
    c: Coincident(g19,g16)
    c: Vertical(g19)
    c: Coincident(g19,g20)
    c: Coincident(g20,g17)
    c: Horizontal(g20)
    c: Coincident(g20,g21)
    c: Coincident(g21,g18)
    c: Coincident(g21,g22)
    c: Coincident(g22,g19)
    c: Horizontal(g22)
    c: Coincident(g23,g15)
    c: Coincident(g23,g4)
    c: Coincident(g23,g24)
    c: Coincident(g24,g16)
    c: DistanceX(g15,g4) = 7.62
    c: Equal(g23,g24)
    c: Angle(g20,g21) = 1.5708
    c: Distance(g19) = 40
    c: Coincident(g25,g18)
    c: Coincident(g25,g6)
    c: Coincident(g25,g26)
    c: Coincident(g26,g17)
    c: DistanceX(g6,g18) = 7.62
FEATURE [Sketcher::SketchObject] Sketch010  label="ButtonHoles"
  ArcFitTolerance = 1e-06
  AttachmentSupport = -> [DatumPlane001]
  ExternalGeometry = -> [Sketch009]
  FullyConstrained = true
  MakeInternals = false
  MapMode = 5
  Placement = pos=(0,-30.9314,90.2338) rot=(1,0,0;2.0944rad)
  sketch-geometry (3):
    g0: Circle CenterX=30 CenterY=-30.9314 CenterZ=0 NormalX=0 NormalY=0 NormalZ=1 AngleXU=0 Radius=7.5
    g1: Circle CenterX=49.84 CenterY=-30.9314 CenterZ=0 NormalX=0 NormalY=0 NormalZ=1 AngleXU=0 Radius=7.5
    g2: Circle CenterX=69.68 CenterY=-30.9314 CenterZ=0 NormalX=0 NormalY=0 NormalZ=1 AngleXU=0 Radius=7.5
  constraints (6):
    c: Coincident(g0,g-3)
    c: Equal(g0,g-3)
    c: Coincident(g1,g-4)
    c: Equal(g1,g-4)
    c: Coincident(g2,g-5)
    c: Equal(g2,g-5)
FEATURE [PartDesign::Pocket] Pocket005
  BaseFeature = -> Pocket
  Direction = (0,0.866025,0.5)
  Length = 3
  Length2 = 5
  Placement = pos=(0,0,0) rot=(1,1,1;2.0944rad)
  Profile = -> Sketch010
  ReferenceAxis = -> Sketch010 [N_Axis]
  Refine = true
  Reversed = true
  Suppressed = false
  Type = 0
  expr: Length = <<HousingSS>>.case_thickness
FEATURE [PartDesign::Fillet] Fillet
  Base = -> Pocket005 [Edge1]
  BaseFeature = -> Pocket005
  Placement = pos=(0,0,0) rot=(1,1,1;2.0944rad)
  Radius = 1
  Refine = true
  SupportTransform = false
  Suppressed = false
  UseAllEdges = false
FEATURE [PartDesign::Fillet] Fillet001
  Base = -> Fillet [Edge53]
  BaseFeature = -> Fillet
  Placement = pos=(0,0,0) rot=(1,1,1;2.0944rad)
  Radius = 1
  Refine = true
  SupportTransform = false
  Suppressed = false
  UseAllEdges = false
FEATURE [PartDesign::Fillet] Fillet002
  Base = -> Fillet001 [Edge1]
  BaseFeature = -> Fillet001
  Placement = pos=(0,0,0) rot=(1,1,1;2.0944rad)
  Radius = 1
  Refine = true
  SupportTransform = false
  Suppressed = false
  UseAllEdges = false
FEATURE [PartDesign::Fillet] Fillet003
  Base = -> Fillet002 [Edge28]
  BaseFeature = -> Fillet002
  Placement = pos=(0,0,0) rot=(1,1,1;2.0944rad)
  Radius = 1
  Refine = true
  SupportTransform = false
  Suppressed = false
  UseAllEdges = false
FEATURE [PartDesign::Fillet] Fillet004
  Base = -> Fillet003 [Edge4]
  BaseFeature = -> Fillet003
  Placement = pos=(0,0,0) rot=(1,1,1;2.0944rad)
  Radius = 1
  Refine = true
  SupportTransform = false
  Suppressed = false
  UseAllEdges = false
FEATURE [PartDesign::AdditiveCone] Cone
  Angle = 360
  AttacherType = Attacher::AttachEngine3D
  AttachmentSupport = -> [Sketch008]
  BaseFeature = -> Fillet004
  Height = 4
  MapMode = 11
  Placement = pos=(13,-64.5,3) rot=(0,0,1;1.5708rad)
  Radius1 = 8
  Radius2 = 3.5
  Refine = true
  Suppressed = false
  expr: Radius2 = <<HousingSS>>.threaded_insert_diameter / 2 + 1 mm
FEATURE [PartDesign::Plane] DatumPlane006  label="BoardYPlane"
  AttachmentOffset = pos=(0,0,0) rot=(0.57735,0.57735,0.57735;2.0944rad)
  AttachmentSupport = -> [Sketch008]
  Length = 138.632
  MapMode = 7
  Placement = pos=(47,-11.4999,3) rot=(0,1,0;4.71239rad)
  ResizeMode = 0
  Width = 142.172
FEATURE [PartDesign::Plane] DatumPlane007  label="BoardXPlane"
  AttachmentOffset = pos=(0,0,0) rot=(0.57735,0.57735,0.57735;2.0944rad)
  AttachmentSupport = -> [Sketch008]
  Length = 130.415
  MapMode = 7
  Placement = pos=(13,-38,3) rot=(0.57735,-0.57735,0.57735;2.0944rad)
  ResizeMode = 0
  Width = 65.1812
FEATURE [Mesh::Feature] Mesh  label="LeftBody (Meshed)"
FEATURE [PartDesign::Hole] Hole
  BaseFeature = -> Cone
  CustomThreadClearance = 0
  Depth = 4
  DepthType = 0
  Diameter = 3.5
  DrillForDepth = false
  DrillPoint = 0
  DrillPointAngle = 118
  HoleCutCountersinkAngle = 90
  HoleCutCustomValues = false
  HoleCutDepth = 0
  HoleCutDiameter = 6.1
  HoleCutType = 0
  ModelThread = false
  Placement = pos=(13,-64.5,3) rot=(0,0,1;1.5708rad)
  Profile = -> Cone [Edge119]
  Refine = true
  Suppressed = false
  Tapered = false
  TaperedAngle = 90
  ThreadClass = 0
  ThreadDepth = 4
  ThreadDepthType = 0
  ThreadDirection = 0
  ThreadFit = 0
  ThreadSize = 0
  ThreadType = 0
  Threaded = false
  UseCustomThreadClearance = false
  expr: Depth = <<HousingSS>>.threaded_insert_depth
  expr: Diameter = <<HousingSS>>.threaded_insert_diameter / 2 + 1 mm
FEATURE [PartDesign::Mirrored] Mirrored
  MirrorPlane = -> DatumPlane006
  Placement = pos=(13,-64.5,3) rot=(0,0,1;1.5708rad)
  Refine = true
  Suppressed = false
  TransformMode = 0
FEATURE [PartDesign::Mirrored] Mirrored001
  MirrorPlane = -> DatumPlane007
  Placement = pos=(13,-64.5,3) rot=(0,0,1;1.5708rad)
  Refine = true
  Suppressed = false
  TransformMode = 0
FEATURE [PartDesign::MultiTransform] MultiTransform
  BaseFeature = -> Hole
  Originals = -> [Cone,Hole]
  Placement = pos=(13,-64.5,3) rot=(0,0,1;1.5708rad)
  Refine = true
  Suppressed = false
  TransformMode = 0
  Transformations = -> [Mirrored,Mirrored001]
FEATURE [PartDesign::Body] Body  label="HousingBody"
  AllowCompound = false
  Configuration = 0
  Group = -> [Sketch,Sketch001,Pad,Sketch002,DatumPlane,Pocket,DatumPlane001,Sketch003,DatumPlane004,Sketch008,DatumPlane005,Sketch009,Sketch010,Pocket005,Fillet,Fillet001,Fillet002,Fillet003,Fillet004,Cone,DatumPlane006,DatumPlane007,Hole,MultiTransform,Mirrored,Mirrored001]
  Origin = -> Origin
  Tip = -> MultiTransform
  expr: .Configuration.Enum = Spreadsheet.cells[<<A3:|>>]
FEATURE [PartDesign::FeatureBase] Clone
  BaseFeature = -> Body
  Suppressed = false
FEATURE [PartDesign::Plane] DatumPlane002  label="SplitPlane"
  AttachmentOffset = pos=(0,0,165) rot=(0,0,1;0rad)
  AttachmentSupport = -> [Clone]
  Length = 60
  MapMode = 4
  Placement = pos=(165,0,0) rot=(0.57735,0.57735,0.57735;2.0944rad)
  ResizeMode = 0
  Width = 60
  expr: .AttachmentOffset.Base.z = <<HousingSS>>.split_offset
FEATURE [Sketcher::SketchObject] Sketch004  label="RightCutSketch"
  ArcFitTolerance = 1e-06
  AttachmentSupport = -> [DatumPlane002]
  ExternalGeometry = -> [Binder]
  FullyConstrained = true
  MakeInternals = false
  MapMode = 5
  Placement = pos=(165,0,0) rot=(0.57735,0.57735,0.57735;2.0944rad)
  sketch-geometry (5):
    g0: LineSegment StartX=-93.7738 StartY=0 StartZ=0 EndX=-60.9314 EndY=90.2338 EndZ=0
    g1: LineSegment StartX=-60.9314 StartY=90.2338 StartZ=0 EndX=-30.9314 EndY=90.2338 EndZ=0
    g2: LineSegment StartX=-30.9314 StartY=90.2338 StartZ=0 EndX=7.1e-15 EndY=36.659 EndZ=0
    g3: LineSegment StartX=7.1e-15 StartY=36.659 StartZ=0 EndX=0 EndY=0 EndZ=0
    g4: LineSegment StartX=0 StartY=0 StartZ=0 EndX=-93.7738 EndY=0 EndZ=0
  constraints (10):
    c: Coincident(g0,g-6)
    c: Coincident(g0,g-3)
    c: Coincident(g0,g1)
    c: Coincident(g1,g-4)
    c: Coincident(g1,g2)
    c: Coincident(g2,g-5)
    c: Coincident(g2,g3)
    c: Coincident(g3,g-1)
    c: Coincident(g3,g4)
    c: Coincident(g4,g0)
FEATURE [PartDesign::Pocket] Pocket001  label="RightCut"
  BaseFeature = -> Clone
  Direction = (-1,0,0)
  Length = 165
  Length2 = 5
  Profile = -> Sketch004
  ReferenceAxis = -> Sketch004 [N_Axis]
  Refine = true
  Reversed = true
  Suppressed = false
  Type = 0
  expr: Length = <<HousingSS>>.housing_width - <<HousingSS>>.split_offset
FEATURE [Sketcher::SketchObject] Sketch005  label="OverlapCutSketch"
  ArcFitTolerance = 1e-06
  AttachmentSupport = -> [DatumPlane002]
  ExternalGeometry = -> [Binder]
  FullyConstrained = true
  MakeInternals = false
  MapMode = 5
  Placement = pos=(165,0,0) rot=(0.57735,0.57735,0.57735;2.0944rad)
  sketch-geometry (5):
    g0: LineSegment StartX=-59.8811 StartY=88.7338 StartZ=0 EndX=-31.7975 EndY=88.7338 EndZ=0
    g1: LineSegment StartX=-31.7975 StartY=88.7338 StartZ=0 EndX=-1.5 EndY=36.257 EndZ=0
    g2: LineSegment StartX=-1.5 StartY=36.257 StartZ=0 EndX=-1.5 EndY=1.5 EndZ=0
    g3: LineSegment StartX=-1.5 StartY=1.5 StartZ=0 EndX=-91.6316 EndY=1.5 EndZ=0
    g4: LineSegment StartX=-91.6316 StartY=1.5 StartZ=0 EndX=-59.8811 EndY=88.7338 EndZ=0
  constraints (10):
    c: Coincident(g0,g-8)
    c: Coincident(g0,g-7)
    c: Coincident(g0,g1)
    c: Coincident(g1,g-6)
    c: Coincident(g1,g2)
    c: Coincident(g2,g-5)
    c: Coincident(g2,g3)
    c: Coincident(g3,g-4)
    c: Coincident(g3,g4)
    c: Coincident(g4,g0)
FEATURE [PartDesign::Pocket] Pocket002
  BaseFeature = -> Pocket001
  Direction = (-1,0,0)
  Length = 10
  Length2 = 5
  Profile = -> Sketch005
  ReferenceAxis = -> Sketch005 [N_Axis]
  Refine = true
  Suppressed = false
  Type = 0
  expr: Length = <<HousingSS>>.split_overlap
FEATURE [PartDesign::Body] Body001  label="LeftBody"
  AllowCompound = false
  Group = -> [Clone,Binder,DatumPlane002,Sketch004,Pocket001,Sketch005,Pocket002]
  Origin = -> Origin001
  Tip = -> Pocket002
FEATURE [PartDesign::FeatureBase] Clone001  label="HousingClone"
  BaseFeature = -> Body
  Suppressed = false
FEATURE [PartDesign::Plane] DatumPlane003
  AttachmentOffset = pos=(0,0,155) rot=(0,0,1;0rad)
  AttachmentSupport = -> [Clone001]
  Length = 60
  MapMode = 4
  Placement = pos=(155,0,0) rot=(0.57735,0.57735,0.57735;2.0944rad)
  ResizeMode = 0
  Width = 60
  expr: .AttachmentOffset.Base.z = <<HousingSS>>.split_offset - <<HousingSS>>.split_overlap
FEATURE [Sketcher::SketchObject] Sketch006  label="LeftCutSketch"
  ArcFitTolerance = 1e-06
  AttachmentSupport = -> [DatumPlane003]
  ExternalGeometry = -> [Binder001]
  FullyConstrained = true
  MakeInternals = false
  MapMode = 5
  Placement = pos=(155,0,0) rot=(0.57735,0.57735,0.57735;2.0944rad)
  sketch-geometry (5):
    g0: LineSegment StartX=-93.7738 StartY=0 StartZ=0 EndX=-60.9314 EndY=90.2338 EndZ=0
    g1: LineSegment StartX=-60.9314 StartY=90.2338 StartZ=0 EndX=-30.9314 EndY=90.2338 EndZ=0
    g2: LineSegment StartX=-30.9314 StartY=90.2338 StartZ=0 EndX=7.1e-15 EndY=36.659 EndZ=0
    g3: LineSegment StartX=7.1e-15 StartY=36.659 StartZ=0 EndX=0 EndY=0 EndZ=0
    g4: LineSegment StartX=0 StartY=0 StartZ=0 EndX=-93.7738 EndY=0 EndZ=0
  constraints (10):
    c: Coincident(g0,g-6)
    c: Coincident(g0,g-3)
    c: Coincident(g0,g1)
    c: Coincident(g1,g-4)
    c: Coincident(g1,g2)
    c: Coincident(g2,g-5)
    c: Coincident(g2,g3)
    c: Coincident(g3,g-1)
    c: Coincident(g3,g4)
    c: Coincident(g4,g0)
FEATURE [PartDesign::Pocket] Pocket003  label="LeftCut"
  BaseFeature = -> Clone001
  Direction = (-1,0,0)
  Length = 165
  Length2 = 5
  Profile = -> Sketch006
  ReferenceAxis = -> Sketch006 [N_Axis]
  Refine = true
  Suppressed = false
  Type = 0
  expr: Length = <<HousingSS>>.split_offset
FEATURE [Sketcher::SketchObject] Sketch007  label="OverlapCutSketch001"
  ArcFitTolerance = 1e-06
  AttachmentSupport = -> [DatumPlane003]
  ExternalGeometry = -> [Binder001]
  FullyConstrained = true
  MakeInternals = false
  MapMode = 5
  Placement = pos=(155,0,0) rot=(0.57735,0.57735,0.57735;2.0944rad)
  sketch-geometry (14):
    g0: LineSegment StartX=-62.6759 StartY=85.4407 StartZ=0 EndX=-60.9314 EndY=90.2338 EndZ=0
    g1: LineSegment StartX=-60.9314 StartY=90.2338 StartZ=0 EndX=-30.9314 EndY=90.2338 EndZ=0
    g2: LineSegment StartX=-30.9314 StartY=90.2338 StartZ=0 EndX=7.1e-15 EndY=36.659 EndZ=0
    g3: LineSegment StartX=7.1e-15 StartY=36.659 StartZ=0 EndX=0 EndY=0 EndZ=0
    g4: LineSegment StartX=0 StartY=0 StartZ=0 EndX=-93.7738 EndY=0 EndZ=0
    g5: LineSegment StartX=-93.7738 StartY=0 StartZ=0 EndX=-90.0376 EndY=10.2653 EndZ=0
    g6: LineSegment StartX=-90.0376 StartY=10.2653 StartZ=0 EndX=-88.628 EndY=9.75231 EndZ=0
    g7: LineSegment StartX=-88.628 StartY=9.75231 StartZ=0 EndX=-91.6316 EndY=1.5 EndZ=0
    g8: LineSegment StartX=-91.6316 StartY=1.5 StartZ=0 EndX=-1.5 EndY=1.5 EndZ=0
    g9: LineSegment StartX=-1.5 StartY=1.5 StartZ=0 EndX=-1.5 EndY=36.257 EndZ=0
    g10: LineSegment StartX=-1.5 StartY=36.257 StartZ=0 EndX=-31.7975 EndY=88.7338 EndZ=0
    g11: LineSegment StartX=-31.7975 StartY=88.7338 StartZ=0 EndX=-59.8811 EndY=88.7338 EndZ=0
    g12: LineSegment StartX=-59.8811 StartY=88.7338 StartZ=0 EndX=-61.2664 EndY=84.9277 EndZ=0
    g13: LineSegment StartX=-61.2664 StartY=84.9277 StartZ=0 EndX=-62.6759 EndY=85.4407 EndZ=0
  constraints (28):
    c: Coincident(g0,g-14)
    c: Coincident(g0,g-13)
    c: Coincident(g0,g1)
    c: Coincident(g1,g-12)
    c: Coincident(g1,g2)
    c: Coincident(g2,g-11)
    c: Coincident(g2,g3)
    c: Coincident(g3,g-1)
    c: Coincident(g3,g4)
    c: Coincident(g4,g-10)
    c: Coincident(g4,g5)
    c: Coincident(g5,g-9)
    c: Coincident(g5,g6)
    c: Coincident(g6,g-8)
    c: Coincident(g6,g7)
    c: Coincident(g7,g-7)
    c: Coincident(g7,g8)
    c: Coincident(g8,g-15)
    c: Coincident(g8,g9)
    c: Coincident(g9,g-6)
    c: Coincident(g9,g10)
    c: Coincident(g10,g-5)
    c: Coincident(g10,g11)
    c: Coincident(g11,g-4)
    c: Coincident(g11,g12)
    c: Coincident(g12,g-3)
    c: Coincident(g12,g13)
    c: Coincident(g13,g0)
FEATURE [PartDesign::Pocket] Pocket004
  BaseFeature = -> Pocket003
  Direction = (-1,0,0)
  Length = 10
  Length2 = 5
  Profile = -> Sketch007
  ReferenceAxis = -> Sketch007 [N_Axis]
  Refine = true
  Reversed = true
  Suppressed = false
  Type = 0
  expr: Length = <<HousingSS>>.split_overlap
FEATURE [PartDesign::Body] Body002  label="RightBody"
  AllowCompound = false
  Group = -> [Clone001,DatumPlane003,Sketch006,Binder001,Pocket003,Sketch007,Pocket004]
  Origin = -> Origin002
  Tip = -> Pocket004
